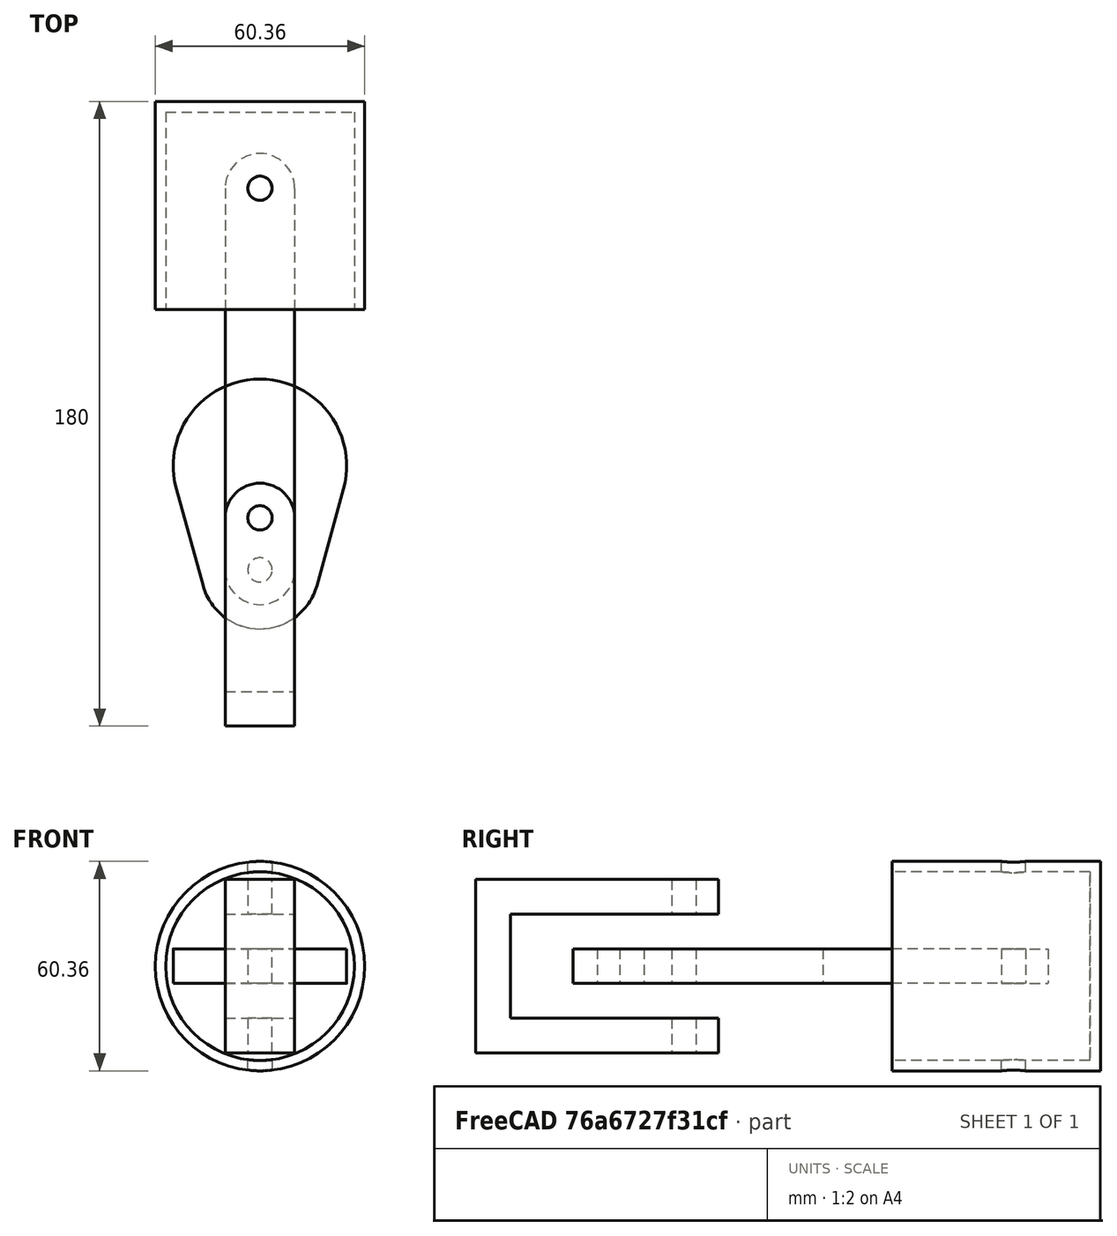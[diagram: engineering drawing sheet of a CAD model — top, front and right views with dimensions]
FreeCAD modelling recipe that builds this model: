
FCSTD DOCUMENT  (FreeCAD 1.0R39319 (Git))
Label: piston_head_assembly
License: All rights reserved
LicenseURL: https://en.wikipedia.org/wiki/All_rights_reserved
objects: Sketcher::SketchObject×7, App::FeaturePython×6, App::Link×5, PartDesign::SubShapeBinder×4, PartDesign::Body×4, PartDesign::Pad×3, PartDesign::Pocket×2, PartDesign::Revolution×1, Assembly::JointGroup×1, Assembly::AssemblyObject×1
note: 40 computed .brp shape members not serialized (recipe doc carries the construction recipe); baked Part::Feature solids carry a one-line shape summary decoded from their .brp

FEATURE [Sketcher::SketchObject] Sketch  label="Master_Sketch"
  ArcFitTolerance = 1e-06
  AttachmentSupport = -> [XY_Plane002]
  FullyConstrained = true
  MakeInternals = false
  MapMode = 5
  sketch-geometry (19):
    g0: ArcOfCircle CenterX=-1e-16 CenterY=55 CenterZ=0 NormalX=0 NormalY=0 NormalZ=1 AngleXU=0 Radius=10 StartAngle=0 EndAngle=3.14159
    g1: ArcOfCircle CenterX=1e-16 CenterY=-55 CenterZ=0 NormalX=0 NormalY=0 NormalZ=1 AngleXU=0 Radius=10 StartAngle=3.14159 EndAngle=6.28319
    g2: LineSegment StartX=10 StartY=55 StartZ=0 EndX=10 EndY=-55 EndZ=0
    g3: LineSegment StartX=-10 StartY=55 StartZ=0 EndX=-10 EndY=-55 EndZ=0
    g4: Circle CenterX=-1e-16 CenterY=55 CenterZ=0 NormalX=0 NormalY=0 NormalZ=1 AngleXU=0 Radius=3.5
    g5: Circle CenterX=1e-16 CenterY=-55 CenterZ=0 NormalX=0 NormalY=0 NormalZ=1 AngleXU=0 Radius=3.5
    g6: ArcOfCircle CenterX=0 CenterY=-25 CenterZ=0 NormalX=0 NormalY=0 NormalZ=1 AngleXU=0 Radius=25 StartAngle=6.01325 EndAngle=9.69471
    g7: ArcOfCircle CenterX=0 CenterY=-55 CenterZ=0 NormalX=0 NormalY=0 NormalZ=1 AngleXU=0 Radius=17 StartAngle=3.41153 EndAngle=6.01325
    g8: LineSegment StartX=-24.0947 StartY=-31.6667 StartZ=0 EndX=-16.3844 EndY=-59.5333 EndZ=0
    g9: LineSegment StartX=24.0947 StartY=-31.6667 StartZ=0 EndX=16.3844 EndY=-59.5333 EndZ=0
    g10: Circle CenterX=0 CenterY=-40 CenterZ=0 NormalX=0 NormalY=0 NormalZ=1 AngleXU=0 Radius=3.5
    g11: ArcOfCircle CenterX=0 CenterY=-40 CenterZ=0 NormalX=0 NormalY=0 NormalZ=1 AngleXU=0 Radius=10 StartAngle=6.28318 EndAngle=9.42478
    g12: LineSegment StartX=-10 StartY=-40 StartZ=0 EndX=-10 EndY=-100 EndZ=0
    g13: LineSegment StartX=-10 StartY=-100 StartZ=0 EndX=10 EndY=-100 EndZ=0
    g14: LineSegment StartX=10 StartY=-40 StartZ=0 EndX=10 EndY=-100 EndZ=0
    g15: LineSegment StartX=-30.18 StartY=80 StartZ=0 EndX=-30.18 EndY=20 EndZ=0
    g16: LineSegment StartX=-30.18 StartY=20 StartZ=0 EndX=29.82 EndY=20 EndZ=0
    g17: LineSegment StartX=29.82 StartY=20 StartZ=0 EndX=29.82 EndY=80 EndZ=0
    g18: LineSegment StartX=29.82 StartY=80 StartZ=0 EndX=-30.18 EndY=80 EndZ=0
  constraints (50):
    c: Tangent(g0,g2) = 1.5708
    c: Tangent(g0,g3) = -1.5708
    c: Tangent(g1,g2) = 1.5708
    c: Tangent(g1,g3) = -1.5708
    c: Equal(g0,g1)
    c: Vertical(g3)
    c: Coincident(g4,g0)
    c: Diameter(g4) = 7
    c: Coincident(g5,g1)
    c: Diameter(g5) = 7
    c: DistanceY(g1,g0) = 110
    c: Radius(g0) = 10
    c: Symmetric(g0,g1,g-1)
    c: PointOnObject(g6,g-2)
    c: PointOnObject(g7,g-2)
    c: Tangent(g8,g6) = -1.5708
    c: Tangent(g8,g7) = -1.5708
    c: Tangent(g9,g7) = 1.5708
    c: Tangent(g9,g6) = 1.5708
    c: DistanceY(g7,g6) = 30
    c: Radius(g6) = 25
    c: Radius(g7) = 17
    c: PointOnObject(g-1,g6)
    c: PointOnObject(g10,g-2)
    c: Coincident(g11,g10)
    c: PointOnObject(g11,g2)
    c: PointOnObject(g11,g3)
    c: Horizontal(g11,g10)
    c: Diameter(g10) = 7
    c: Coincident(g12,g11)
    c: Vertical(g12)
    c: Distance(g10,g13) = 60
    c: Coincident(g12,g13)
    c: Coincident(g14,g13)
    c: Horizontal(g13)
    c: Vertical(g14)
    c: DistanceY(g10,g6) = 15
    c: Coincident(g11,g14)
    c: Coincident(g15,g16)
    c: Coincident(g16,g17)
    c: Coincident(g17,g18)
    c: Coincident(g18,g15)
    c: Vertical(g15)
    c: Vertical(g17)
    c: Horizontal(g16)
    c: Horizontal(g18)
    c: DistanceX(g18,g18) = 60
    c: DistanceY(g15,g15) = 60
    c: Distance(g-1,g16) = 20
    c: Distance(g-2,g15) = 30.18
FEATURE [PartDesign::SubShapeBinder] Binder
  BindCopyOnChange = 0
  BindMode = 0
  ClaimChildren = false
  Context = -> Body [Binder.]
  Fuse = false
  MakeFace = false
  OffsetFill = false
  OffsetIntersection = false
  OffsetJoinType = 0
  OffsetOpenResult = false
  PartialLoad = false
  Refine = true
  Relative = true
  Support = -> [Sketch]
  _Version = 2
FEATURE [Sketcher::SketchObject] Sketch001
  ArcFitTolerance = 1e-06
  AttachmentSupport = -> [XY_Plane]
  ExternalGeometry = -> [Binder]
  FullyConstrained = true
  MakeInternals = false
  MapMode = 5
  sketch-geometry (6):
    g0: LineSegment StartX=-10 StartY=55 StartZ=0 EndX=-10 EndY=-55 EndZ=0
    g1: LineSegment StartX=10 StartY=55 StartZ=0 EndX=10 EndY=-55 EndZ=0
    g2: ArcOfCircle CenterX=-1e-16 CenterY=55 CenterZ=0 NormalX=0 NormalY=0 NormalZ=1 AngleXU=0 Radius=10 StartAngle=2e-16 EndAngle=3.14159
    g3: ArcOfCircle CenterX=1e-16 CenterY=-55 CenterZ=0 NormalX=0 NormalY=0 NormalZ=1 AngleXU=0 Radius=10 StartAngle=3.14159 EndAngle=6.28319
    g4: Circle CenterX=-1e-16 CenterY=55 CenterZ=0 NormalX=0 NormalY=0 NormalZ=1 AngleXU=0 Radius=3.5
    g5: Circle CenterX=1e-16 CenterY=-55 CenterZ=0 NormalX=0 NormalY=0 NormalZ=1 AngleXU=0 Radius=3.5
  constraints (14):
    c: Coincident(g2,g-6)
    c: Coincident(g2,g1)
    c: Coincident(g2,g0)
    c: Coincident(g3,g-8)
    c: Coincident(g3,g1)
    c: Coincident(g3,g0)
    c: Coincident(g4,g2)
    c: Coincident(g5,g3)
    c: Equal(g-4,g1)
    c: Coincident(g-4,g1)
    c: Coincident(g-7,g0)
    c: Equal(g-6,g4)
    c: Equal(g5,g-8)
    c: Equal(g-5,g0)
FEATURE [PartDesign::Pad] Pad
  Direction = (0,0,1)
  Length = 10
  Length2 = 10
  Midplane = true
  Profile = -> Sketch001
  ReferenceAxis = -> Sketch001 [N_Axis]
  Refine = true
  Suppressed = false
  Type = 0
FEATURE [PartDesign::Body] Body  label="Link"
  AllowCompound = false
  Group = -> [Binder,Sketch001,Pad]
  Origin = -> Origin
  Tip = -> Pad
FEATURE [PartDesign::SubShapeBinder] Binder001
  BindCopyOnChange = 0
  BindMode = 0
  ClaimChildren = false
  Context = -> Body001 [Binder001.]
  Fuse = false
  MakeFace = false
  OffsetFill = false
  OffsetIntersection = false
  OffsetJoinType = 0
  OffsetOpenResult = false
  PartialLoad = false
  Refine = true
  Relative = true
  Support = -> [Sketch]
  _Version = 2
FEATURE [Sketcher::SketchObject] Sketch002
  ArcFitTolerance = 1e-06
  AttachmentSupport = -> [XY_Plane001]
  ExternalGeometry = -> [Binder001]
  FullyConstrained = true
  MakeInternals = false
  MapMode = 5
  sketch-geometry (6):
    g0: LineSegment StartX=-30.18 StartY=20 StartZ=0 EndX=-30.18 EndY=80 EndZ=0
    g1: LineSegment StartX=-30.18 StartY=80 StartZ=0 EndX=0 EndY=80 EndZ=0
    g2: LineSegment StartX=0 StartY=80 StartZ=0 EndX=0 EndY=77 EndZ=0
    g3: LineSegment StartX=0 StartY=77 StartZ=0 EndX=-27.18 EndY=77 EndZ=0
    g4: LineSegment StartX=-27.18 StartY=77 StartZ=0 EndX=-27.18 EndY=20 EndZ=0
    g5: LineSegment StartX=-27.18 StartY=20 StartZ=0 EndX=-30.18 EndY=20 EndZ=0
  constraints (17):
    c: Coincident(g-5,g0)
    c: Coincident(g0,g-4)
    c: Coincident(g0,g1)
    c: Horizontal(g1)
    c: Coincident(g2,g3)
    c: Horizontal(g3)
    c: Coincident(g3,g4)
    c: PointOnObject(g4,g-5)
    c: Vertical(g4)
    c: Coincident(g4,g5)
    c: Coincident(g5,g0)
    c: Vertical(g2)
    c: PointOnObject(g1,g2)
    c: PointOnObject(g1,g-2)
    c: Distance(g0,g4) = 3
    c: Distance(g3,g1) = 3
    c: DistanceY(g2,g2) = 3
FEATURE [PartDesign::Revolution] Revolution
  Angle = 360
  Angle2 = 60
  Axis = (0,1,0)
  Base = (0,0,0)
  Profile = -> Sketch002
  ReferenceAxis = -> Sketch002 [V_Axis]
  Refine = true
  Suppressed = false
  Type = 0
FEATURE [Sketcher::SketchObject] Sketch003
  ArcFitTolerance = 1e-06
  AttachmentSupport = -> [XY_Plane001]
  ExternalGeometry = -> [Binder001]
  FullyConstrained = true
  MakeInternals = false
  MapMode = 5
  sketch-geometry (1):
    g0: Circle CenterX=0 CenterY=55 CenterZ=0 NormalX=0 NormalY=0 NormalZ=1 AngleXU=0 Radius=3.5
  constraints (2):
    c: Coincident(g0,g-3)
    c: Equal(g0,g-3)
FEATURE [PartDesign::SubShapeBinder] Binder002
  BindCopyOnChange = 0
  BindMode = 0
  ClaimChildren = false
  Context = -> Body002 [Binder002.]
  Fuse = false
  MakeFace = false
  OffsetFill = false
  OffsetIntersection = false
  OffsetJoinType = 0
  OffsetOpenResult = false
  PartialLoad = false
  Refine = true
  Relative = true
  Support = -> [Sketch]
  _Version = 2
FEATURE [Sketcher::SketchObject] Sketch004
  ArcFitTolerance = 1e-06
  AttachmentSupport = -> [XY_Plane002]
  ExternalGeometry = -> [Binder002]
  FullyConstrained = true
  MakeInternals = false
  MapMode = 5
  sketch-geometry (6):
    g0: Circle CenterX=0 CenterY=-40 CenterZ=0 NormalX=0 NormalY=0 NormalZ=1 AngleXU=0 Radius=3.5
    g1: Circle CenterX=0 CenterY=-55 CenterZ=0 NormalX=0 NormalY=0 NormalZ=1 AngleXU=0 Radius=3.5
    g2: LineSegment StartX=-24.0947 StartY=-31.6667 StartZ=0 EndX=-16.3844 EndY=-59.5333 EndZ=0
    g3: ArcOfCircle CenterX=2e-16 CenterY=-55 CenterZ=0 NormalX=0 NormalY=0 NormalZ=1 AngleXU=0 Radius=17 StartAngle=3.41153 EndAngle=6.01325
    g4: LineSegment StartX=16.3844 StartY=-59.5333 StartZ=0 EndX=24.0947 EndY=-31.6667 EndZ=0
    g5: ArcOfCircle CenterX=1.2308e-12 CenterY=-25 CenterZ=0 NormalX=0 NormalY=0 NormalZ=1 AngleXU=0 Radius=25 StartAngle=6.01325 EndAngle=9.69471
  constraints (12):
    c: Coincident(g0,g-7)
    c: Equal(g0,g-7)
    c: Coincident(g1,g-8)
    c: Equal(g1,g-8)
    c: Coincident(g-5,g2)
    c: Coincident(g2,g-6)
    c: Tangent(g2,g3) = -1.5708
    c: Coincident(g3,g-6)
    c: Tangent(g3,g4) = -1.5708
    c: Tangent(g4,g5) = -1.5708
    c: Coincident(g5,g2)
    c: PointOnObject(g-1,g5)
FEATURE [PartDesign::Pad] Pad001
  Direction = (0,0,1)
  Length = 10
  Length2 = 10
  Midplane = true
  Profile = -> Sketch004
  ReferenceAxis = -> Sketch004 [N_Axis]
  Refine = true
  Suppressed = false
  Type = 0
FEATURE [PartDesign::Body] Body002  label="Crank"
  AllowCompound = false
  Group = -> [Binder002,Sketch004,Pad001]
  Origin = -> Origin002
  Tip = -> Pad001
FEATURE [PartDesign::SubShapeBinder] Binder003
  BindCopyOnChange = 0
  BindMode = 0
  ClaimChildren = false
  Context = -> Body003 [Binder003.]
  Fuse = false
  MakeFace = false
  OffsetFill = false
  OffsetIntersection = false
  OffsetJoinType = 0
  OffsetOpenResult = false
  PartialLoad = false
  Refine = true
  Relative = true
  Support = -> [Sketch]
  _Version = 2
FEATURE [Sketcher::SketchObject] Sketch005
  ArcFitTolerance = 1e-06
  AttachmentSupport = -> [XY_Plane003]
  ExternalGeometry = -> [Binder003]
  FullyConstrained = true
  MakeInternals = false
  MapMode = 5
  sketch-geometry (5):
    g0: LineSegment StartX=-10 StartY=-40 StartZ=0 EndX=-10 EndY=-100 EndZ=0
    g1: LineSegment StartX=-10 StartY=-100 StartZ=0 EndX=10 EndY=-100 EndZ=0
    g2: LineSegment StartX=10 StartY=-100 StartZ=0 EndX=10 EndY=-40 EndZ=0
    g3: ArcOfCircle CenterX=-3.5369e-11 CenterY=-40 CenterZ=0 NormalX=0 NormalY=0 NormalZ=1 AngleXU=0 Radius=10 StartAngle=0 EndAngle=3.14159
    g4: Circle CenterX=-3.5369e-11 CenterY=-40 CenterZ=0 NormalX=0 NormalY=0 NormalZ=1 AngleXU=0 Radius=3.49997
  constraints (10):
    c: Tangent(g-6,g0) = -1.5708
    c: Coincident(g0,g1)
    c: Coincident(g1,g-4)
    c: Horizontal(g1)
    c: Coincident(g1,g2)
    c: Coincident(g2,g-6)
    c: Tangent(g2,g3) = -1.5708
    c: Coincident(g3,g0)
    c: Coincident(g4,g3)
    c: Tangent(g4,g-7)
FEATURE [PartDesign::Pad] Pad002
  Direction = (0,0,1)
  Length = 50
  Length2 = 10
  Midplane = true
  Profile = -> Sketch005
  ReferenceAxis = -> Sketch005 [N_Axis]
  Refine = true
  Suppressed = false
  Type = 0
FEATURE [Sketcher::SketchObject] Sketch006
  ArcFitTolerance = 1e-06
  AttachmentSupport = -> [Pad002]
  ExternalGeometry = -> [Pad002]
  FullyConstrained = true
  MakeInternals = false
  MapMode = 5
  Placement = pos=(-10,7.1e-15,0) rot=(0.57735,-0.57735,-0.57735;2.0944rad)
  sketch-geometry (4):
    g0: LineSegment StartX=25 StartY=15 StartZ=0 EndX=25 EndY=-15 EndZ=0
    g1: LineSegment StartX=25 StartY=-15 StartZ=0 EndX=90 EndY=-15 EndZ=0
    g2: LineSegment StartX=90 StartY=-15 StartZ=0 EndX=90 EndY=15 EndZ=0
    g3: LineSegment StartX=90 StartY=15 StartZ=0 EndX=25 EndY=15 EndZ=0
  constraints (12):
    c: Coincident(g0,g1)
    c: Coincident(g1,g2)
    c: Coincident(g2,g3)
    c: Coincident(g3,g0)
    c: Vertical(g0)
    c: Vertical(g2)
    c: Horizontal(g1)
    c: Horizontal(g3)
    c: Distance(g1,g3) = 30
    c: DistanceX(g2,g-3) = 10
    c: DistanceY(g2,g-3) = 10
    c: DistanceX(g0,g2) = 65
FEATURE [PartDesign::Pocket] Pocket001
  BaseFeature = -> Pad002
  Direction = (1,0,0)
  Length = 5
  Length2 = 5
  Midplane = true
  Profile = -> Sketch006
  ReferenceAxis = -> Sketch006 [N_Axis]
  Refine = true
  Suppressed = false
  Type = 1
FEATURE [PartDesign::Body] Body003  label="mount"
  AllowCompound = false
  Group = -> [Binder003,Sketch005,Pad002,Sketch006,Pocket001]
  Origin = -> Origin003
  Tip = -> Pocket001
FEATURE [PartDesign::Pocket] Pocket
  BaseFeature = -> Revolution
  Direction = (0,0,-1)
  Length = 5
  Length2 = 5
  Midplane = true
  Profile = -> Sketch003
  ReferenceAxis = -> Sketch003 [N_Axis]
  Refine = true
  Suppressed = false
  Type = 1
FEATURE [PartDesign::Body] Body001  label="Piston Head"
  AllowCompound = false
  Group = -> [Binder001,Sketch002,Revolution,Sketch003,Pocket]
  Origin = -> Origin001
  Tip = -> Pocket
FEATURE [App::Link] mount  label="mount001"
  LinkedObject = -> Body003
FEATURE [App::FeaturePython] GroundedJoint  # Assembly grounded joint (typed FeaturePython)
  ObjectToGround = -> mount
FEATURE [App::Link] Crank  label="Crank001"
  LinkPlacement = pos=(-17.7353,-75.8533,-10) rot=(0,0,1;2.68222rad)
  LinkedObject = -> Body002
  Placement = pos=(-17.7353,-75.8533,-10) rot=(0,0,1;2.68222rad)
FEATURE [App::Link] Crank001  label="Crank002"
  LinkPlacement = pos=(-17.7353,-75.8533,10) rot=(0,0,1;2.68222rad)
  LinkedObject = -> Body002
  Placement = pos=(-17.7353,-75.8533,10) rot=(0,0,1;2.68222rad)
FEATURE [App::FeaturePython] Joint  label="Revolute"  # Assembly joint (typed FeaturePython)
  Activated = true
  AngleMax = 0
  AngleMin = 0
  Detach1 = false
  Detach2 = false
  Distance = 0
  Distance2 = 0
  EnableAngleMax = false
  EnableAngleMin = false
  EnableLengthMax = false
  EnableLengthMin = false
  JointType = 1 (Revolute)
  LengthMax = 0
  LengthMin = 0
  Offset2 = pos=(0,0,-10) rot=(0,0,1;0rad)
  Placement1 = pos=(-3.6e-15,-40,5) rot=(0,0,1;0rad)
  Placement2 = pos=(-3.5369e-11,-40,-5) rot=(1,0,0;3.14159rad)
  Reference1 = -> Assembly [Crank.Edge18,Crank.Edge18]
  Reference2 = -> Assembly [mount.Edge27,mount.Edge27]
FEATURE [App::Link] Link  label="Link001"
  LinkPlacement = pos=(3.32538,28.3443,1.4e-15) rot=(0,0,1;0.060498rad)
  LinkedObject = -> Body
  Placement = pos=(3.32538,28.3443,1.4e-15) rot=(0,0,1;0.060498rad)
FEATURE [App::FeaturePython] Joint001  label="Revolute001"  # Assembly joint (typed FeaturePython)
  Activated = true
  AngleMax = 0
  AngleMin = 0
  Detach1 = false
  Detach2 = false
  Distance = 0
  Distance2 = 0
  EnableAngleMax = false
  EnableAngleMin = false
  EnableLengthMax = false
  EnableLengthMin = false
  JointType = 1 (Revolute)
  LengthMax = 0
  LengthMin = 0
  Offset2 = pos=(0,0,-10) rot=(0,0,1;0rad)
  Placement1 = pos=(0,-55,5) rot=(0,0,1;0rad)
  Placement2 = pos=(0,-55,-5) rot=(0,0,1;0rad)
  Reference1 = -> Assembly [Crank.Edge15,Crank.Edge15]
  Reference2 = -> Assembly [Link.Edge15,Link.Edge15]
FEATURE [App::FeaturePython] Joint002  label="Fixed"  # Assembly joint (typed FeaturePython)
  Activated = true
  AngleMax = 0
  AngleMin = 0
  Detach1 = false
  Detach2 = false
  Distance = 0
  Distance2 = 0
  EnableAngleMax = false
  EnableAngleMin = false
  EnableLengthMax = false
  EnableLengthMin = false
  JointType = 0 (Fixed)
  LengthMax = 0
  LengthMin = 0
  Offset2 = pos=(0,0,20) rot=(0,0,1;0rad)
  Placement1 = pos=(5.755e-13,-33.696,5) rot=(0,0,1;0rad)
  Placement2 = pos=(5.684e-13,-33.696,25) rot=(0,0,1;0rad)
  Reference1 = -> Assembly [Crank001.Face8,Crank001.Face8]
  Reference2 = -> Assembly [Crank.Face8,Crank.Face8]
FEATURE [App::Link] Piston_Head  label="Piston Head001"
  LinkPlacement = pos=(-1.77068e-11,28.0004,1.09906) rot=(1,0,0;0.008586rad)
  LinkedObject = -> Body001
  Placement = pos=(-1.77068e-11,28.0004,1.09906) rot=(1,0,0;0.008586rad)
FEATURE [App::FeaturePython] Joint003  label="Revolute002"  # Assembly joint (typed FeaturePython)
  Activated = true
  AngleMax = 0
  AngleMin = 0
  Detach1 = false
  Detach2 = false
  Distance = 0
  Distance2 = 0
  EnableAngleMax = false
  EnableAngleMin = false
  EnableLengthMax = false
  EnableLengthMin = false
  JointType = 1 (Revolute)
  LengthMax = 0
  LengthMin = 0
  Offset2 = pos=(0,0,-27) rot=(0,0,1;0rad)
  Placement1 = pos=(0,55,-28.5723) rot=(0,0,1;0rad)
  Placement2 = pos=(0,55,-27) rot=(0,0,1;0rad)
  Reference1 = -> Assembly [Piston_Head.Face5,Piston_Head.Face5]
  Reference2 = -> Assembly [Link.Face6,Link.Face6]
FEATURE [App::FeaturePython] Joint004  label="Slider"  # Assembly joint (typed FeaturePython)
  Activated = true
  AngleMax = 0
  AngleMin = 0
  Detach1 = false
  Detach2 = false
  Distance = 0
  Distance2 = 0
  EnableAngleMax = false
  EnableAngleMin = false
  EnableLengthMax = false
  EnableLengthMin = false
  JointType = 3 (Slider)
  LengthMax = 0
  LengthMin = 0
  Placement1 = pos=(0,80,-2e-16) rot=(0,0.707107,0.707107;3.14159rad)
  Placement2 = pos=(-1.77068e-11,-100,0) rot=(-1,0,0;1.5708rad)
  Reference1 = -> Assembly [Piston_Head.Face2,Piston_Head.Face2]
  Reference2 = -> Assembly [mount.Face3,mount.Face3]
FEATURE [Assembly::JointGroup] Joints
  Group = -> [GroundedJoint,Joint,Joint001,Joint002,Joint003,Joint004]
FEATURE [Assembly::AssemblyObject] Assembly
  Group = -> [Joints,mount,GroundedJoint,Crank,Crank001,Joint,Link,Joint001,Joint002,Piston_Head,Joint003,Joint004]
  Origin = -> Origin004
  Type = Assembly
